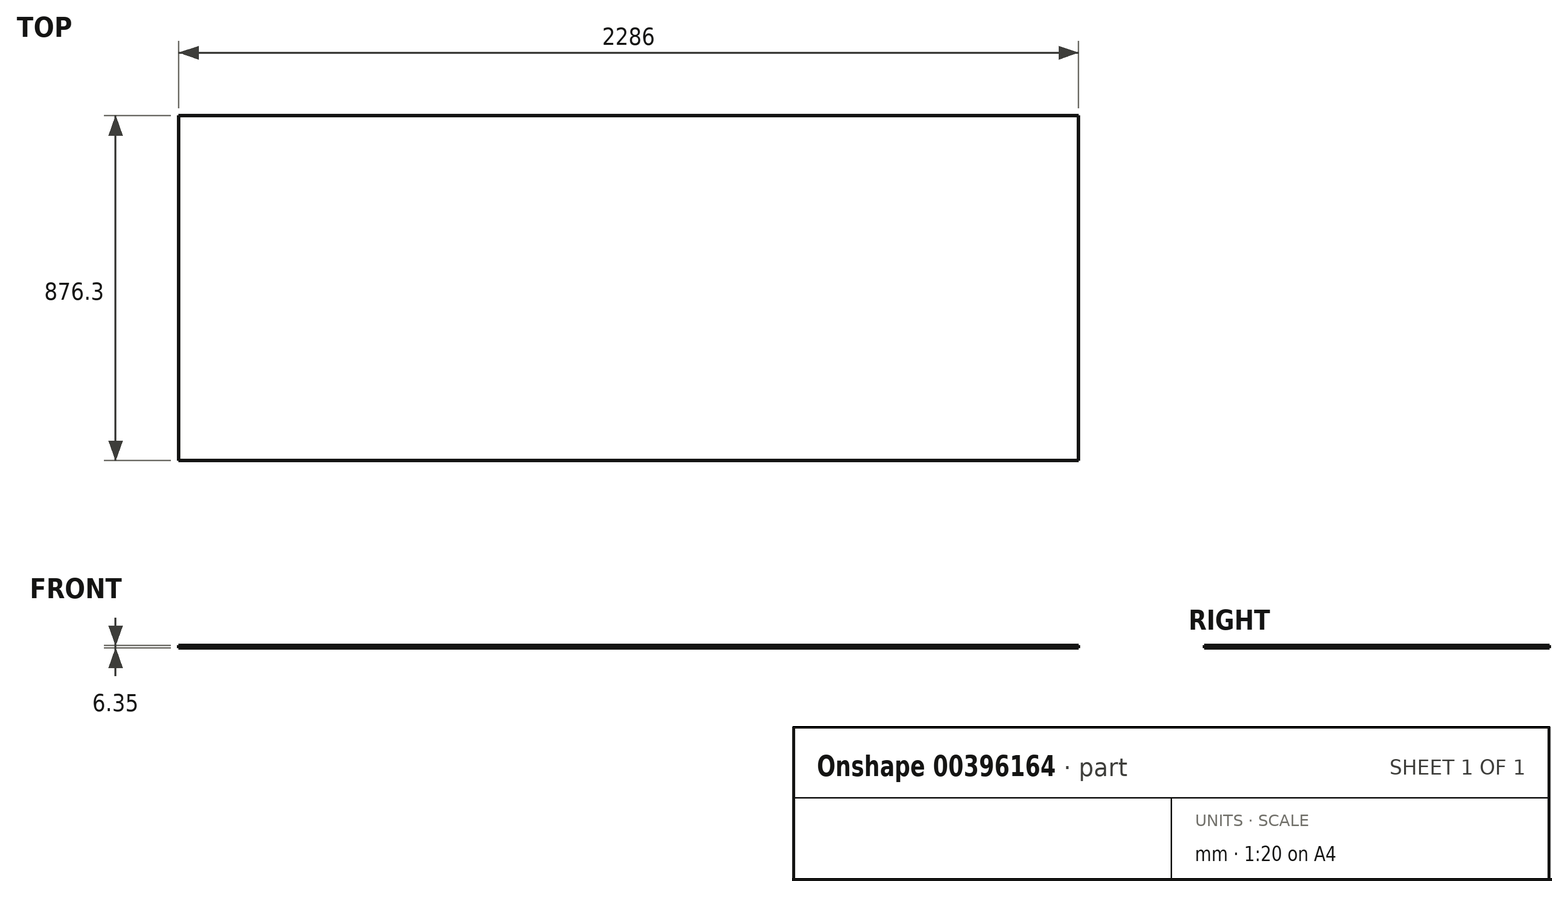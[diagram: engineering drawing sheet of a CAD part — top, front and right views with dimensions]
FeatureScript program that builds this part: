
annotation { "Feature Type Name" : "Feature", "Feature Type Description" : "" }
export const myFeature = defineFeature(function(context is Context, id is Id, definition is map)
    precondition{}
    {
        {
            var Q0;
            Q0=qCreatedBy(makeId("Right.planeOp"),FACE);
            var sketch = newSketch(context, id + "F0", { "sketchPlane" : qUnion([Q0])});
            skLineSegment(sketch, "E0.bottom", {"start": v(427.27, -47.06) * mm, "end": v(-449.03, -47.06) * mm});
            skLineSegment(sketch, "E0.top", {"start": v(427.27, -40.71) * mm, "end": v(-449.03, -40.71) * mm});
            skLineSegment(sketch, "E0.left", {"start": v(427.27, -47.06) * mm, "end": v(427.27, -40.71) * mm});
            skLineSegment(sketch, "E0.right", {"start": v(-449.03, -47.06) * mm, "end": v(-449.03, -40.71) * mm});
            skPoint(sketch, "E0.middle", {"position": v(-10.88, -43.89) * mm});
            skSolve(sketch);
        }
        {
            var Q0;
            Q0=makeQuery(id+"F0.imprint","IMPRINT",FACE,{"disambiguationData":[TD([[makeQuery(id+"F0.imprint","IMPRINT",EDGE,{"derivedFrom":sQuery(id+"F0.wireOp",EDGE,"E0.bottom")}),-1.0]])]});
            extrude(context, id + "F1", {"entities" : qUnion([Q0]), "depth" : 2286 * mm});
        }
    });
